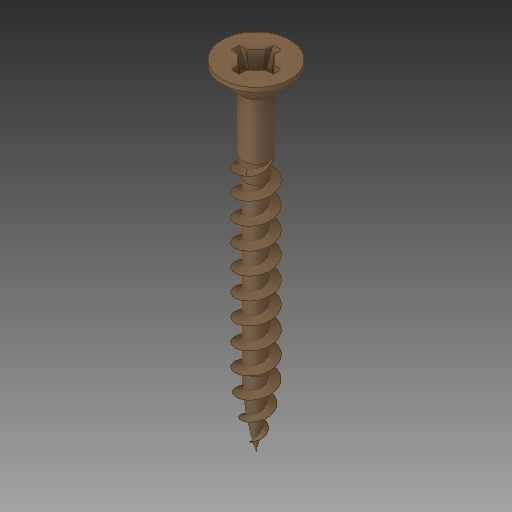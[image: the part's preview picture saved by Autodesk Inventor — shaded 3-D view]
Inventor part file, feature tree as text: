
AUTODESK INVENTOR PART (.ipt)
format: ipt  version: 2018 (Build 220112000, 112)  size: 715,264 bytes
history: native  units: in
note: dims shown in document units (in); Inventor stores cm internally (conversion verified against a paired STEP export)
features: other x1, thread x1
ambient origin geometry x8: Origin, YZ Plane, XZ Plane, XY Plane, X Axis, Y Axis, Z Axis, Center Point
bodies: Solid1 (feature_tree), Solid2 (feature_tree)
feature tree (2):
  parser-record x1  (decoder bookkeeping rows leaked as tree rows — omitted from the tree; the rows remain in map.json)
  thread  "Thread-1"  [1 undecoded]
note: 1 required parameter value undecoded (feature->parameter linkage not recoverable at this tier; creation-order binding heuristic only, values carry confidence <= 0.55)
